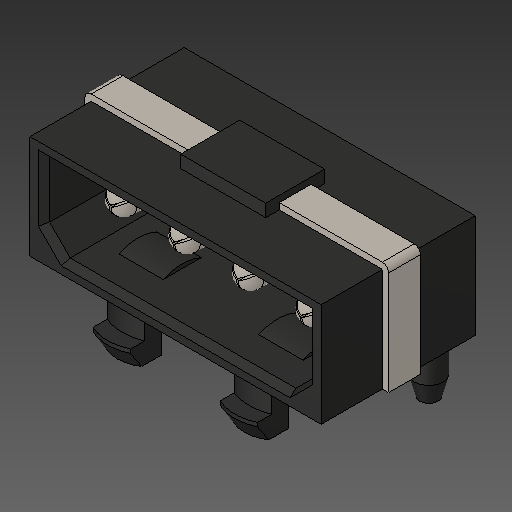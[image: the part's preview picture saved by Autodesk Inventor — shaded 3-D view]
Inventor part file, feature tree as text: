
AUTODESK INVENTOR PART (.ipt)
format: ipt  version: 2018.2 (Build 222227000, 227)  size: 390,144 bytes
history: native  units: mm
features: other x1, fillet x1
ambient origin geometry x8: Origin, YZ Plane, XZ Plane, XY Plane, X Axis, Y Axis, Z Axis, Center Point
bodies: Body1 (feature_tree)
feature tree (2):
  other  "ソリッド1"
  fillet  "Fillet1"  [1 undecoded]
note: 1 required parameter value undecoded (feature->parameter linkage not recoverable at this tier; creation-order binding heuristic only, values carry confidence <= 0.55)
